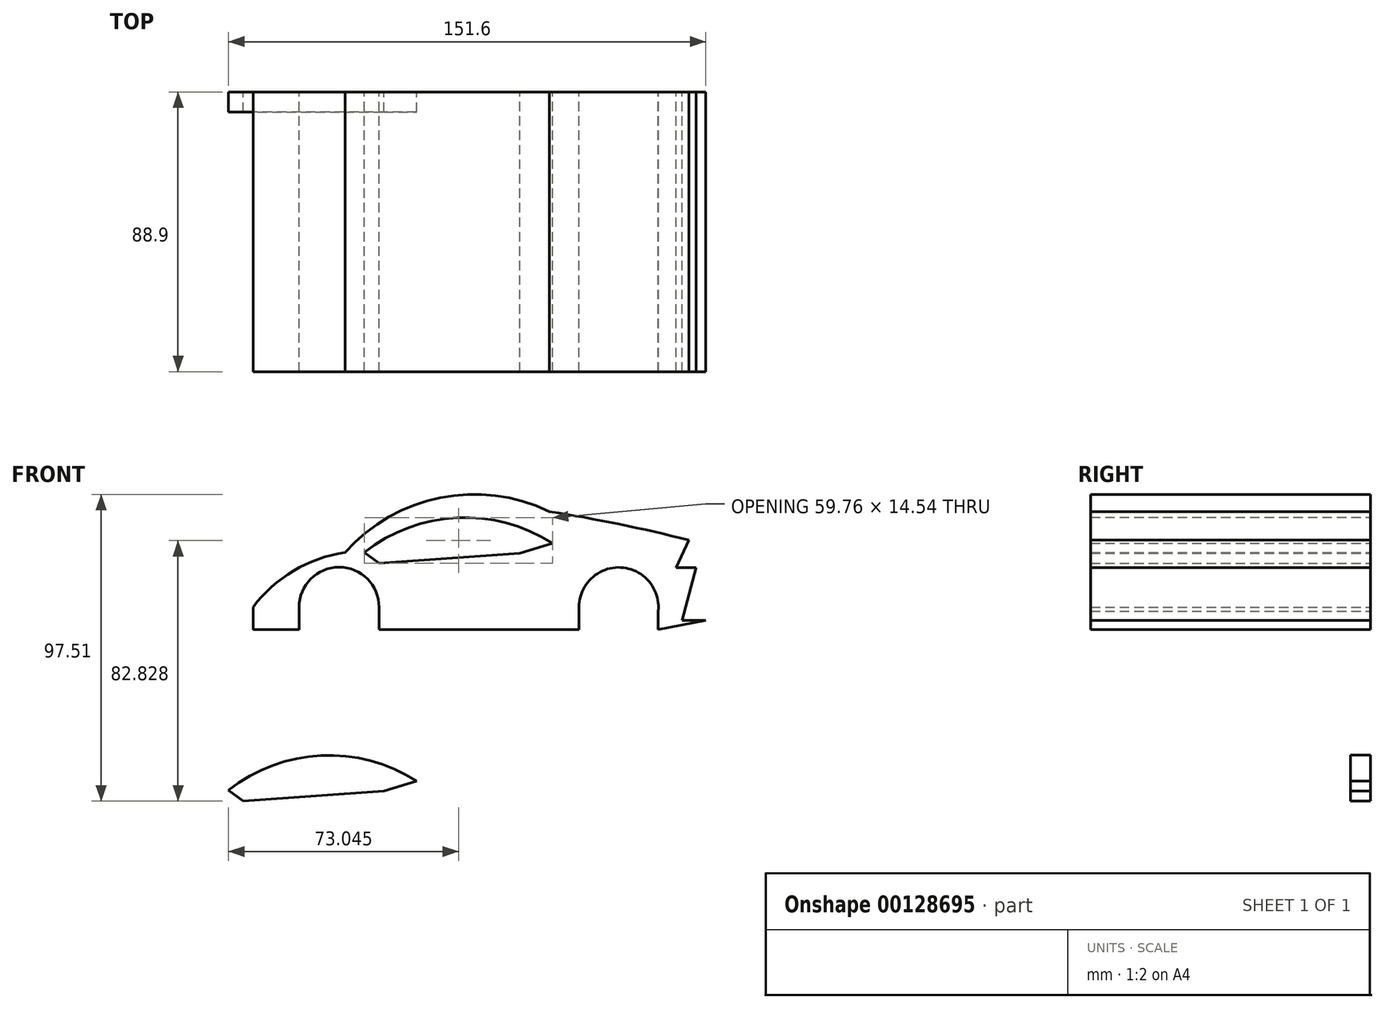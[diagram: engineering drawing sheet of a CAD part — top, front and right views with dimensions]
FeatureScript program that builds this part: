
annotation { "Feature Type Name" : "Feature", "Feature Type Description" : "" }
export const myFeature = defineFeature(function(context is Context, id is Id, definition is map)
    precondition{}
    {
        {
            var Q0;
            Q0=qCreatedBy(makeId("Front.planeOp"),FACE);
            var sketch = newSketch(context, id + "F0", { "sketchPlane" : qUnion([Q0])});
            skLineSegment(sketch, "E0", {"start": v(-44.62, 0) * mm, "end": v(-44.62, 7.1) * mm});
            skLineSegment(sketch, "E1", {"start": v(-19.22, 0) * mm, "end": v(-19.22, 7.1) * mm});
            skArc(sketch, "E2", {"start": v(-19.22, 7.1) * mm, "mid": v(-31.92, 19.8) * mm, "end": v(-44.62, 7.1) * mm});
            skLineSegment(sketch, "E3", {"start": v(-19.22, 0) * mm, "end": v(44.28, 0) * mm});
            skLineSegment(sketch, "E4", {"start": v(69.47, 5.83) * mm, "end": v(69.47, 0) * mm});
            skLineSegment(sketch, "E5", {"start": v(44.28, 7.1) * mm, "end": v(44.28, 0) * mm});
            skArc(sketch, "E6", {"start": v(69.47, 5.83) * mm, "mid": v(57.54, 19.7) * mm, "end": v(44.28, 7.1) * mm});
            skPoint(sketch, "E7.endSnap0", {"position": v(69.47, 2.91) * mm});
            skPoint(sketch, "E8.endSnap0", {"position": v(57.54, 19.7) * mm});
            skLineSegment(sketch, "E9", {"start": v(69.47, 0) * mm, "end": v(84.56, 2.91) * mm});
            skLineSegment(sketch, "E10", {"start": v(84.56, 2.91) * mm, "end": v(77.02, 2.91) * mm});
            skLineSegment(sketch, "E11", {"start": v(77.02, 2.91) * mm, "end": v(81.5, 19.7) * mm});
            skLineSegment(sketch, "E12", {"start": v(81.5, 19.7) * mm, "end": v(75.2, 19.7) * mm});
            skPoint(sketch, "E13.endSnap0", {"position": v(79.26, 11.31) * mm});
            skPoint(sketch, "E14.orphan", {"position": v(57.54, 28.7) * mm});
            skLineSegment(sketch, "E15", {"start": v(79.26, 28.37) * mm, "end": v(75.2, 19.7) * mm});
            skArc(sketch, "E16", {"start": v(34.87, 37.48) * mm, "mid": v(0.22, 41.88) * mm, "end": v(-30.04, 24.45) * mm});
            skArc(sketch, "E17", {"start": v(-30.04, 24.45) * mm, "mid": v(-46.38, 18.67) * mm, "end": v(-59.28, 7.1) * mm});
            skLineSegment(sketch, "E18", {"start": v(-59.28, 7.1) * mm, "end": v(-54.5, 3.55) * mm});
            skPoint(sketch, "E18.endSnap0", {"position": v(-44.62, 3.55) * mm});
            skLineSegment(sketch, "E19", {"start": v(-54.5, 3.55) * mm, "end": v(-59.28, 0) * mm});
            skLineSegment(sketch, "E20", {"start": v(-59.28, 0) * mm, "end": v(-44.62, 0) * mm});
            skLineSegment(sketch, "E21", {"start": v(-23.88, 24.45) * mm, "end": v(-19.22, 21) * mm});
            skLineSegment(sketch, "E22", {"start": v(-19.22, 21) * mm, "end": v(25.52, 24.19) * mm});
            skLineSegment(sketch, "E23", {"start": v(25.52, 24.19) * mm, "end": v(35.88, 27.38) * mm});
            skArc(sketch, "E24", {"start": v(35.88, 27.38) * mm, "mid": v(5.53, 35.54) * mm, "end": v(-23.88, 24.45) * mm});
            skArc(sketch, "E25", {"start": v(79.26, 28.37) * mm, "mid": v(57.17, 33.45) * mm, "end": v(34.87, 37.48) * mm});
            skPoint(sketch, "E26.start.orphan", {"position": v(-15.05, 0) * mm});
            skPoint(sketch, "E27.orphan", {"position": v(38.2, 0) * mm});
            skLineSegment(sketch, "E28.left", {"start": v(-59.28, 0) * mm, "end": v(-59.28, 53.06) * mm});
            skSolve(sketch);
        }
        {
            var Q0;
            Q0 = qSketchRegion(id + "F0", true);
            extrude(context, id + "F1", {"entities" : qUnion([Q0]), "depth" : 88.9 * mm});
        }
        {
            var Q0;
            Q0=qCreatedBy(makeId("Front.planeOp"),FACE);
            var sketch = newSketch(context, id + "F2", { "sketchPlane" : qUnion([Q0])});
            skLineSegment(sketch, "E29", {"start": v(-67.04, -51.1) * mm, "end": v(-62.38, -54.56) * mm});
            skLineSegment(sketch, "E30", {"start": v(-62.38, -54.56) * mm, "end": v(-17.64, -51.37) * mm});
            skLineSegment(sketch, "E31", {"start": v(-17.64, -51.37) * mm, "end": v(-7.28, -48.18) * mm});
            skArc(sketch, "E32", {"start": v(-7.28, -48.18) * mm, "mid": v(-37.63, -40.02) * mm, "end": v(-67.04, -51.1) * mm});
            skSolve(sketch);
        }
        {
            var Q0;
            Q0 = qSketchRegion(id + "F2", true);
            extrude(context, id + "F3", {"entities" : qUnion([Q0]), "depth" : 6.35 * mm});
        }
    });
